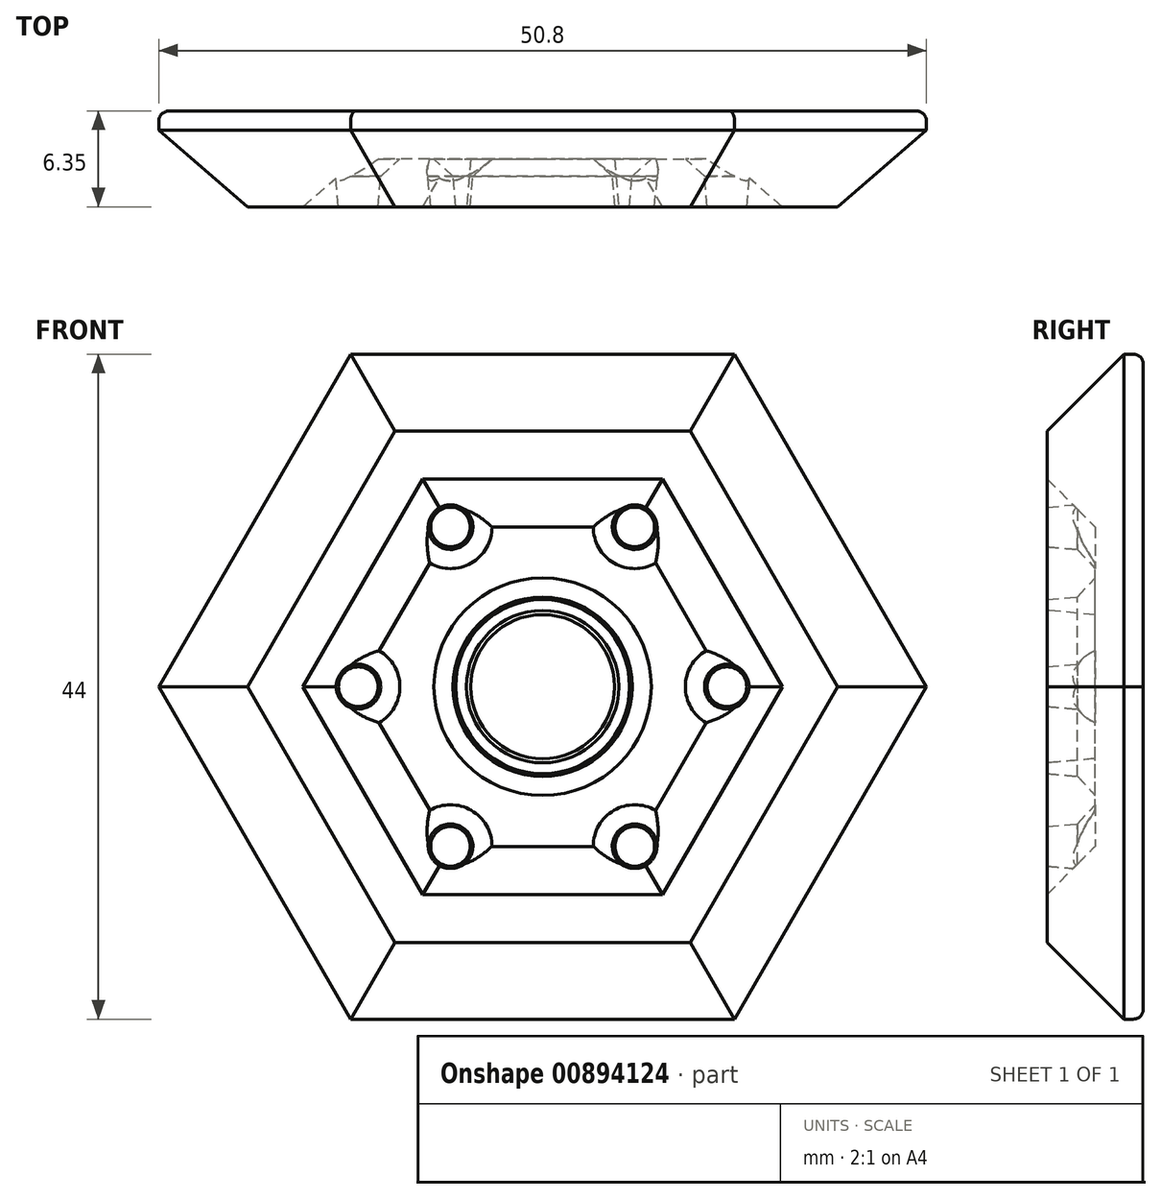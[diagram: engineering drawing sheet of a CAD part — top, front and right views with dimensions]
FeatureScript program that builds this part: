
annotation { "Feature Type Name" : "Feature", "Feature Type Description" : "" }
export const myFeature = defineFeature(function(context is Context, id is Id, definition is map)
    precondition{}
    {
        {
            var Q0;
            Q0=qCreatedBy(makeId("Front.planeOp"),FACE);
            var sketch = newSketch(context, id + "F0", { "sketchPlane" : qUnion([Q0])});
            skLineSegment(sketch, "E0", {"start": v(-25.4, 0) * mm, "end": v(25.4, 0) * mm, "construction": true});
            skLineSegment(sketch, "E1", {"start": v(-25.4, 0) * mm, "end": v(-12.7, -22) * mm});
            skLineSegment(sketch, "E2", {"start": v(-12.7, -22) * mm, "end": v(12.7, -22) * mm});
            skLineSegment(sketch, "E3", {"start": v(12.7, -22) * mm, "end": v(25.4, 0) * mm});
            skLineSegment(sketch, "E4", {"start": v(25.4, 0) * mm, "end": v(12.7, 22) * mm});
            skLineSegment(sketch, "E5", {"start": v(12.7, 22) * mm, "end": v(-12.7, 22) * mm});
            skLineSegment(sketch, "E6", {"start": v(-12.7, 22) * mm, "end": v(-25.4, 0) * mm});
            skPoint(sketch, "E7", {"position": v(0, 0) * mm});
            skSolve(sketch);
        }
        {
            var Q0;
            Q0=makeQuery(id+"F0.imprint","IMPRINT",FACE,{"disambiguationData":[TD([[makeQuery(id+"F0.imprint","IMPRINT",EDGE,{"derivedFrom":sQuery(id+"F0.wireOp",EDGE,"E1")}),1.0]])]});
            extrude(context, id + "F1", {"entities" : qUnion([Q0]), "depth" : 6.35 * mm, "offsetDistance" : 25.4 * mm});
        }
        {
            var Q0;
            Q0=makeQuery(id+"F1.opExtrude","CAP_EDGE",EDGE,{"disambiguationData":[OSD([sQuery(id+"F0.wireOp",EDGE,"E2")])],"isStart":false});
            var Q1;
            Q1=makeQuery(id+"F1.opExtrude","CAP_EDGE",EDGE,{"disambiguationData":[OSD([sQuery(id+"F0.wireOp",EDGE,"E3")])],"isStart":false});
            var Q2;
            Q2=makeQuery(id+"F1.opExtrude","CAP_EDGE",EDGE,{"disambiguationData":[OSD([sQuery(id+"F0.wireOp",EDGE,"E4")])],"isStart":false});
            var Q3;
            Q3=makeQuery(id+"F1.opExtrude","CAP_EDGE",EDGE,{"disambiguationData":[OSD([sQuery(id+"F0.wireOp",EDGE,"E5")])],"isStart":false});
            var Q4;
            Q4=makeQuery(id+"F1.opExtrude","CAP_EDGE",EDGE,{"disambiguationData":[OSD([sQuery(id+"F0.wireOp",EDGE,"E6")])],"isStart":false});
            var Q5;
            Q5=makeQuery(id+"F1.opExtrude","CAP_EDGE",EDGE,{"disambiguationData":[OSD([sQuery(id+"F0.wireOp",EDGE,"E1")])],"isStart":false});
            chamfer(context, id + "F2", {"entities" : qUnion([Q0, Q1, Q2, Q3, Q4, Q5]), "width" : 5.08 * mm, "tangentPropagation" : true});
        }
        {
            var Q0;
            Q0=makeQuery(id+"F1.opExtrude","CAP_FACE",FACE,{"disambiguationData":[OSD([sQuery(id+"F0.wireOp",EDGE,"E1"),sQuery(id+"F0.wireOp",EDGE,"E2"),sQuery(id+"F0.wireOp",EDGE,"E3"),sQuery(id+"F0.wireOp",EDGE,"E4"),sQuery(id+"F0.wireOp",EDGE,"E5"),sQuery(id+"F0.wireOp",EDGE,"E6")])],"isStart":false});
            var sketch = newSketch(context, id + "F3", { "sketchPlane" : qUnion([Q0])});
            skLineSegment(sketch, "E8.0", {"start": v(-7.93, 13.74) * mm, "end": v(-15.87, 0) * mm});
            skLineSegment(sketch, "E8.1", {"start": v(-7.93, -13.74) * mm, "end": v(7.93, -13.74) * mm});
            skLineSegment(sketch, "E8.2", {"start": v(7.93, -13.74) * mm, "end": v(15.87, 0) * mm});
            skLineSegment(sketch, "E8.3", {"start": v(-15.87, 0) * mm, "end": v(-7.93, -13.74) * mm});
            skLineSegment(sketch, "E8.4", {"start": v(15.87, 0) * mm, "end": v(7.93, 13.74) * mm});
            skLineSegment(sketch, "E8.5", {"start": v(7.93, 13.74) * mm, "end": v(-7.93, 13.74) * mm});
            skSolve(sketch);
        }
        {
            var Q0;
            Q0=makeQuery(id+"F3.imprint","IMPRINT",FACE,{"disambiguationData":[TD([[makeQuery(id+"F3.imprint","IMPRINT",EDGE,{"derivedFrom":sQuery(id+"F3.wireOp",EDGE,"E8.0")}),1.0]])]});
            extrude(context, id + "F4", {"entities" : qUnion([Q0]), "operationType" : NewBodyOperationType.REMOVE, "oppositeDirection" : true, "depth" : 3.17 * mm, "offsetDistance" : 25.4 * mm});
        }
        {
            var Q0;
            Q0=makeQuery(id+"F4.boolean.opBoolean","COPY",EDGE,{"derivedFrom":makeQuery(id+"F4.opExtrude","CAP_EDGE",EDGE,{"disambiguationData":[OSD([sQuery(id+"F3.wireOp",EDGE,"E8.0")])],"isStart":false})});
            var Q1;
            Q1=makeQuery(id+"F4.boolean.opBoolean","COPY",EDGE,{"derivedFrom":makeQuery(id+"F4.opExtrude","CAP_EDGE",EDGE,{"disambiguationData":[OSD([sQuery(id+"F3.wireOp",EDGE,"E8.5")])],"isStart":false})});
            var Q2;
            Q2=makeQuery(id+"F4.boolean.opBoolean","COPY",EDGE,{"derivedFrom":makeQuery(id+"F4.opExtrude","CAP_EDGE",EDGE,{"disambiguationData":[OSD([sQuery(id+"F3.wireOp",EDGE,"E8.3")])],"isStart":false})});
            var Q3;
            Q3=makeQuery(id+"F4.boolean.opBoolean","COPY",EDGE,{"derivedFrom":makeQuery(id+"F4.opExtrude","CAP_EDGE",EDGE,{"disambiguationData":[OSD([sQuery(id+"F3.wireOp",EDGE,"E8.1")])],"isStart":false})});
            var Q4;
            Q4=makeQuery(id+"F4.boolean.opBoolean","COPY",EDGE,{"derivedFrom":makeQuery(id+"F4.opExtrude","CAP_EDGE",EDGE,{"disambiguationData":[OSD([sQuery(id+"F3.wireOp",EDGE,"E8.2")])],"isStart":false})});
            var Q5;
            Q5=makeQuery(id+"F4.boolean.opBoolean","COPY",EDGE,{"derivedFrom":makeQuery(id+"F4.opExtrude","CAP_EDGE",EDGE,{"disambiguationData":[OSD([sQuery(id+"F3.wireOp",EDGE,"E8.4")])],"isStart":false})});
            chamfer(context, id + "F5", {"entities" : qUnion([Q0, Q1, Q2, Q3, Q4, Q5]), "width" : 3.17 * mm, "tangentPropagation" : true});
        }
        {
            var Q0;
            Q0=makeQuery(id+"F1.opExtrude","CAP_EDGE",EDGE,{"disambiguationData":[OSD([sQuery(id+"F0.wireOp",EDGE,"E3")])],"isStart":true});
            var Q1;
            Q1=makeQuery(id+"F1.opExtrude","CAP_EDGE",EDGE,{"disambiguationData":[OSD([sQuery(id+"F0.wireOp",EDGE,"E4")])],"isStart":true});
            var Q2;
            Q2=makeQuery(id+"F1.opExtrude","CAP_EDGE",EDGE,{"disambiguationData":[OSD([sQuery(id+"F0.wireOp",EDGE,"E2")])],"isStart":true});
            var Q3;
            Q3=makeQuery(id+"F1.opExtrude","CAP_EDGE",EDGE,{"disambiguationData":[OSD([sQuery(id+"F0.wireOp",EDGE,"E1")])],"isStart":true});
            var Q4;
            Q4=makeQuery(id+"F1.opExtrude","CAP_EDGE",EDGE,{"disambiguationData":[OSD([sQuery(id+"F0.wireOp",EDGE,"E6")])],"isStart":true});
            var Q5;
            Q5=makeQuery(id+"F1.opExtrude","CAP_EDGE",EDGE,{"disambiguationData":[OSD([sQuery(id+"F0.wireOp",EDGE,"E5")])],"isStart":true});
            fillet(context, id + "F6", {"entities" : qUnion([Q0, Q1, Q2, Q3, Q4, Q5]), "radius" : 0.64 * mm, "tangentPropagation" : true, "allowEdgeOverflow" : false});
        }
        {
            var Q0;
            Q0=makeQuery(id+"F4.boolean.opBoolean","COPY",FACE,{"derivedFrom":makeQuery(id+"F4.opExtrude","CAP_FACE",FACE,{"disambiguationData":[OSD([sQuery(id+"F3.wireOp",EDGE,"E8.0"),sQuery(id+"F3.wireOp",EDGE,"E8.1"),sQuery(id+"F3.wireOp",EDGE,"E8.2"),sQuery(id+"F3.wireOp",EDGE,"E8.3"),sQuery(id+"F3.wireOp",EDGE,"E8.4"),sQuery(id+"F3.wireOp",EDGE,"E8.5")])],"isStart":false})});
            var sketch = newSketch(context, id + "F7", { "sketchPlane" : qUnion([Q0])});
            skCircle(sketch, "E9", {"center": v(0, 0) * mm, "radius": 4.76 * mm});
            skCircle(sketch, "E10", {"center": v(12.2, 0) * mm, "radius": 1.59 * mm});
            skCircle(sketch, "E11.0", {"center": v(0, 0) * mm, "radius": 6.03 * mm});
            skCircle(sketch, "E12.1.0", {"center": v(6.1, 10.57) * mm, "radius": 1.59 * mm});
            skCircle(sketch, "E12.2.0", {"center": v(-6.1, 10.57) * mm, "radius": 1.59 * mm});
            skCircle(sketch, "E12.3.0", {"center": v(-12.2, 0) * mm, "radius": 1.59 * mm});
            skCircle(sketch, "E12.4.0", {"center": v(-6.1, -10.57) * mm, "radius": 1.59 * mm});
            skCircle(sketch, "E12.5.0", {"center": v(6.1, -10.57) * mm, "radius": 1.59 * mm});
            skSolve(sketch);
        }
        {
            var Q0;
            Q0 = qSketchRegion(id + "F7", true);
            extrude(context, id + "F8", {"entities" : qUnion([Q0]), "operationType" : NewBodyOperationType.ADD, "depth" : 3.17 * mm, "offsetDistance" : 25.4 * mm, "hasDraft" : true, "draftAngle" : 5 * degree, "draftPullDirection" : true});
        }
        {
            var Q0;
            Q0=makeQuery(id+"F8.opExtrude","CAP_EDGE",EDGE,{"disambiguationData":[OSD([sQuery(id+"F7.wireOp",EDGE,"E9")])],"isStart":true});
            var Q1;
            Q1=makeQuery(id+"F8.opExtrude","CAP_EDGE",EDGE,{"disambiguationData":[OSD([sQuery(id+"F7.wireOp",EDGE,"E11.0")])],"isStart":true});
            var Q2;
            Q2=makeQuery(id+"F8.opExtrude","CAP_EDGE",EDGE,{"disambiguationData":[OSD([sQuery(id+"F7.wireOp",EDGE,"E10")])],"isStart":true});
            var Q3;
            Q3=makeQuery(id+"F8.opExtrude","CAP_EDGE",EDGE,{"disambiguationData":[OSD([sQuery(id+"F7.wireOp",EDGE,"E12.1.0")])],"isStart":true});
            var Q4;
            Q4=makeQuery(id+"F8.opExtrude","CAP_EDGE",EDGE,{"disambiguationData":[OSD([sQuery(id+"F7.wireOp",EDGE,"E12.2.0")])],"isStart":true});
            var Q5;
            Q5=makeQuery(id+"F8.opExtrude","CAP_EDGE",EDGE,{"disambiguationData":[OSD([sQuery(id+"F7.wireOp",EDGE,"E12.3.0")])],"isStart":true});
            var Q6;
            Q6=makeQuery(id+"F8.opExtrude","CAP_EDGE",EDGE,{"disambiguationData":[OSD([sQuery(id+"F7.wireOp",EDGE,"E12.4.0")])],"isStart":true});
            var Q7;
            Q7=makeQuery(id+"F8.opExtrude","CAP_EDGE",EDGE,{"disambiguationData":[OSD([sQuery(id+"F7.wireOp",EDGE,"E12.5.0")])],"isStart":true});
            chamfer(context, id + "F9", {"entities" : qUnion([Q0, Q1, Q2, Q3, Q4, Q5, Q6, Q7]), "width" : 1.27 * mm, "tangentPropagation" : true});
        }
    });
